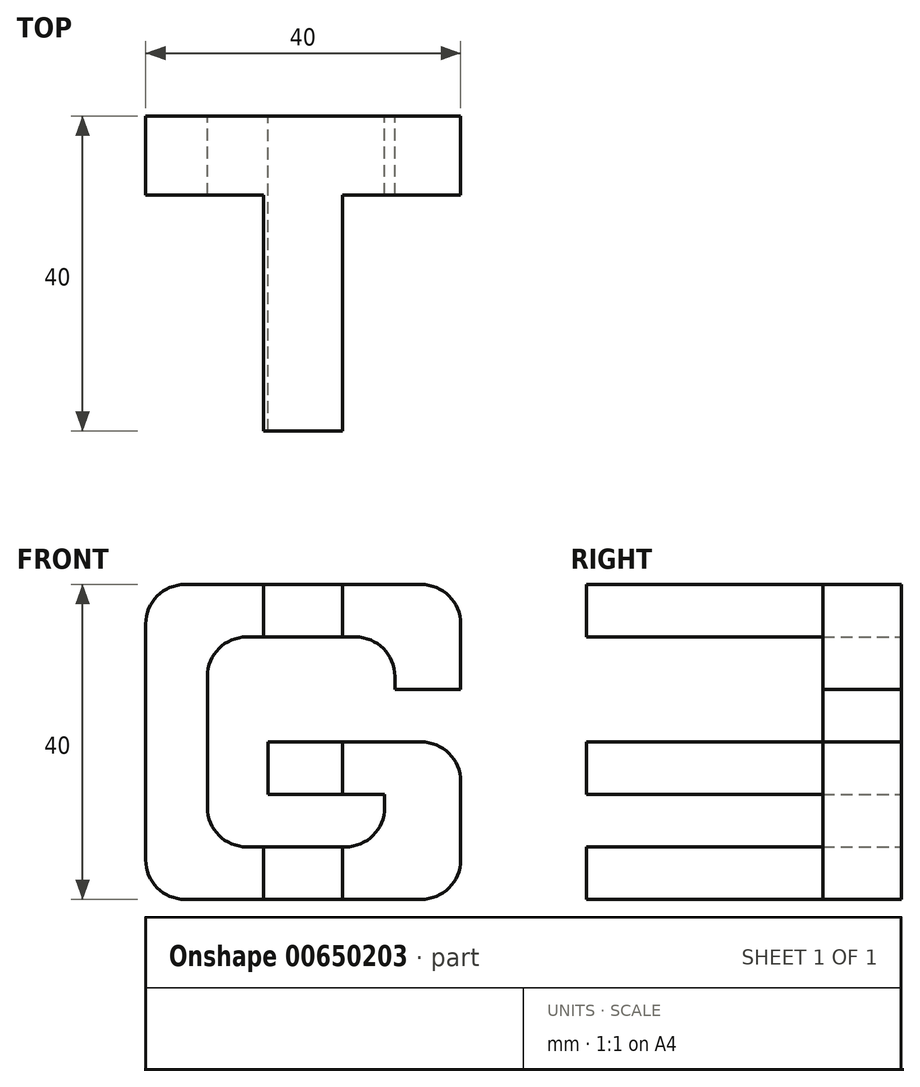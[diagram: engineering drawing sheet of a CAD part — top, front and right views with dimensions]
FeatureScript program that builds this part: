
annotation { "Feature Type Name" : "Feature", "Feature Type Description" : "" }
export const myFeature = defineFeature(function(context is Context, id is Id, definition is map)
    precondition{}
    {
        {
            var Q0;
            Q0=qCreatedBy(makeId("Top.planeOp"),FACE);
            var sketch = newSketch(context, id + "F0", { "sketchPlane" : qUnion([Q0])});
            skLineSegment(sketch, "E0.bottom", {"start": v(20, 20) * mm, "end": v(-20, 20) * mm});
            skLineSegment(sketch, "E0.top", {"start": v(20, -20) * mm, "end": v(-20, -20) * mm});
            skLineSegment(sketch, "E0.left", {"start": v(20, 20) * mm, "end": v(20, -20) * mm});
            skLineSegment(sketch, "E0.right", {"start": v(-20, 20) * mm, "end": v(-20, -20) * mm});
            skPoint(sketch, "E0.middle", {"position": v(0, 0) * mm});
            skSolve(sketch);
        }
        {
            var Q0;
            Q0=makeQuery(id+"F0.imprint","IMPRINT",FACE,{"disambiguationData":[TD([[makeQuery(id+"F0.imprint","IMPRINT",EDGE,{"derivedFrom":sQuery(id+"F0.wireOp",EDGE,"E0.bottom")}),1.0]])]});
            extrude(context, id + "F1", {"entities" : qUnion([Q0]), "endBound" : BoundingType.SYMMETRIC, "depth" : 40 * mm, "offsetDistance" : 25 * mm});
        }
        {
            var Q0;
            Q0=qCreatedBy(makeId("Top.planeOp"),FACE);
            var sketch = newSketch(context, id + "F2", { "sketchPlane" : qUnion([Q0])});
            skPoint(sketch, "E1.middle", {"position": v(0, 0) * mm});
            skLineSegment(sketch, "E2", {"start": v(-20, 20) * mm, "end": v(20, 20) * mm});
            skLineSegment(sketch, "E3", {"start": v(20, 10) * mm, "end": v(5, 10) * mm});
            skLineSegment(sketch, "E4", {"start": v(5, 10) * mm, "end": v(5, -20) * mm});
            skLineSegment(sketch, "E5", {"start": v(5, -20) * mm, "end": v(-5, -20) * mm});
            skLineSegment(sketch, "E6", {"start": v(-5, -20) * mm, "end": v(-5, 10) * mm});
            skLineSegment(sketch, "E7", {"start": v(-5, 10) * mm, "end": v(-20, 10) * mm});
            skLineSegment(sketch, "E8", {"start": v(-20, 10) * mm, "end": v(-20, 20) * mm});
            skLineSegment(sketch, "E9", {"start": v(20, 20) * mm, "end": v(20, 10) * mm});
            skSolve(sketch);
        }
        {
            var Q0;
            Q0 = qSketchRegion(id + "F2", true);
            extrude(context, id + "F3", {"entities" : qUnion([Q0]), "operationType" : NewBodyOperationType.INTERSECT, "endBound" : BoundingType.SYMMETRIC, "depth" : 40 * mm, "offsetDistance" : 25 * mm});
        }
        {
            var Q0;
            Q0=qCreatedBy(makeId("Right.planeOp"),FACE);
            var sketch = newSketch(context, id + "F4", { "sketchPlane" : qUnion([Q0])});
            skLineSegment(sketch, "E10", {"start": v(-20, 20) * mm, "end": v(20, 20) * mm});
            skLineSegment(sketch, "E11", {"start": v(20, 20) * mm, "end": v(20, -20) * mm});
            skLineSegment(sketch, "E12", {"start": v(20, -20) * mm, "end": v(12, -20) * mm});
            skLineSegment(sketch, "E13", {"start": v(12, -20) * mm, "end": v(12, 10) * mm});
            skLineSegment(sketch, "E14", {"start": v(12, 10) * mm, "end": v(4, 10) * mm});
            skLineSegment(sketch, "E15", {"start": v(4, 10) * mm, "end": v(4, -5) * mm});
            skLineSegment(sketch, "E16", {"start": v(4, -5) * mm, "end": v(-4, -5) * mm});
            skLineSegment(sketch, "E17", {"start": v(-4, -5) * mm, "end": v(-4, 10) * mm});
            skLineSegment(sketch, "E18", {"start": v(-4, 10) * mm, "end": v(-12, 10) * mm});
            skLineSegment(sketch, "E19", {"start": v(-12, 10) * mm, "end": v(-12, -20) * mm});
            skLineSegment(sketch, "E20", {"start": v(-12, -20) * mm, "end": v(-20, -20) * mm});
            skLineSegment(sketch, "E21", {"start": v(-20, -20) * mm, "end": v(-20, 20) * mm});
            skSolve(sketch);
        }
        {
            var Q0;
            Q0=qCreatedBy(makeId("Front.planeOp"),FACE);
            var sketch = newSketch(context, id + "F5", { "sketchPlane" : qUnion([Q0])});
            skLineSegment(sketch, "E22", {"start": v(-15, 20) * mm, "end": v(15, 20) * mm});
            skLineSegment(sketch, "E23", {"start": v(20, 15) * mm, "end": v(20, 6.67) * mm});
            skLineSegment(sketch, "E24", {"start": v(20, 6.67) * mm, "end": v(11.65, 6.67) * mm});
            skLineSegment(sketch, "E25", {"start": v(11.65, 6.67) * mm, "end": v(11.65, 8.33) * mm});
            skLineSegment(sketch, "E26", {"start": v(6.65, 13.33) * mm, "end": v(-7.16, 13.33) * mm});
            skLineSegment(sketch, "E27", {"start": v(-12.16, 8.33) * mm, "end": v(-12.16, -8.33) * mm});
            skLineSegment(sketch, "E28", {"start": v(-7.16, -13.33) * mm, "end": v(5.37, -13.33) * mm});
            skLineSegment(sketch, "E29", {"start": v(10.37, -8.33) * mm, "end": v(10.37, -6.67) * mm});
            skLineSegment(sketch, "E30", {"start": v(10.37, -6.67) * mm, "end": v(-4.47, -6.67) * mm});
            skLineSegment(sketch, "E31", {"start": v(-4.47, -6.67) * mm, "end": v(-4.47, 0) * mm});
            skLineSegment(sketch, "E32", {"start": v(-4.47, 0) * mm, "end": v(15, 0) * mm});
            skLineSegment(sketch, "E33", {"start": v(20, -5) * mm, "end": v(20, -15) * mm});
            skLineSegment(sketch, "E34", {"start": v(15, -20) * mm, "end": v(-15, -20) * mm});
            skLineSegment(sketch, "E35", {"start": v(-20, -15) * mm, "end": v(-20, 15) * mm});
            skPoint(sketch, "E36.visualSharp", {"position": v(-12.16, 13.33) * mm});
            skArc(sketch, "E36.filletArc", {"start": v(-7.16, 13.33) * mm, "mid": v(-10.7, 11.87) * mm, "end": v(-12.16, 8.33) * mm});
            skPoint(sketch, "E37.visualSharp", {"position": v(-12.16, -13.33) * mm});
            skArc(sketch, "E37.filletArc", {"start": v(-12.16, -8.33) * mm, "mid": v(-10.7, -11.87) * mm, "end": v(-7.16, -13.33) * mm});
            skPoint(sketch, "E38.visualSharp", {"position": v(10.37, -13.33) * mm});
            skArc(sketch, "E38.filletArc", {"start": v(5.37, -13.33) * mm, "mid": v(8.9, -11.87) * mm, "end": v(10.37, -8.33) * mm});
            skPoint(sketch, "E39.visualSharp", {"position": v(11.65, 13.33) * mm});
            skArc(sketch, "E39.filletArc", {"start": v(11.65, 8.33) * mm, "mid": v(10.18, 11.87) * mm, "end": v(6.65, 13.33) * mm});
            skPoint(sketch, "E40.visualSharp", {"position": v(-20, 20) * mm});
            skArc(sketch, "E40.filletArc", {"start": v(-15, 20) * mm, "mid": v(-18.54, 18.54) * mm, "end": v(-20, 15) * mm});
            skPoint(sketch, "E41.visualSharp", {"position": v(-20, -20) * mm});
            skArc(sketch, "E41.filletArc", {"start": v(-20, -15) * mm, "mid": v(-18.54, -18.54) * mm, "end": v(-15, -20) * mm});
            skPoint(sketch, "E42.visualSharp", {"position": v(20, -20) * mm});
            skArc(sketch, "E42.filletArc", {"start": v(15, -20) * mm, "mid": v(18.54, -18.54) * mm, "end": v(20, -15) * mm});
            skPoint(sketch, "E43.visualSharp", {"position": v(20, 0) * mm});
            skArc(sketch, "E43.filletArc", {"start": v(20, -5) * mm, "mid": v(18.54, -1.46) * mm, "end": v(15, 0) * mm});
            skPoint(sketch, "E44.visualSharp", {"position": v(20, 20) * mm});
            skArc(sketch, "E44.filletArc", {"start": v(20, 15) * mm, "mid": v(18.54, 18.54) * mm, "end": v(15, 20) * mm});
            skSolve(sketch);
        }
        {
            var Q0;
            Q0 = qSketchRegion(id + "F5", true);
            extrude(context, id + "F6", {"entities" : qUnion([Q0]), "operationType" : NewBodyOperationType.INTERSECT, "endBound" : BoundingType.SYMMETRIC, "depth" : 40 * mm, "offsetDistance" : 25 * mm});
        }
    });
